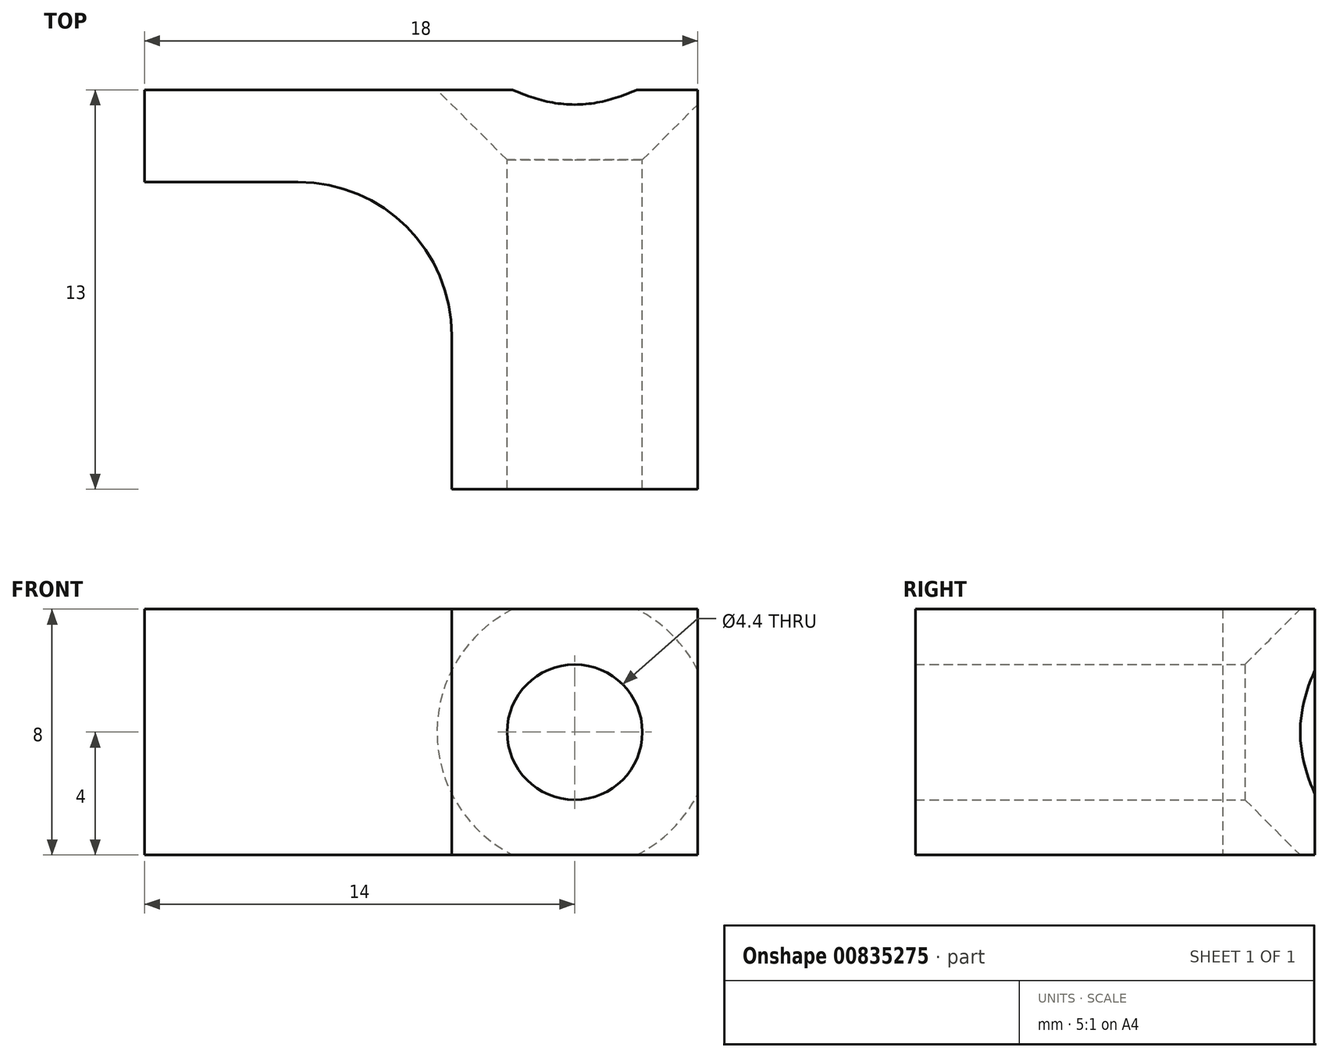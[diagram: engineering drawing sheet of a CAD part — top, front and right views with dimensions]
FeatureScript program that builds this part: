
annotation { "Feature Type Name" : "Feature", "Feature Type Description" : "" }
export const myFeature = defineFeature(function(context is Context, id is Id, definition is map)
    precondition{}
    {
        {
            var Q0;
            Q0=qCreatedBy(makeId("Top.planeOp"),FACE);
            var sketch = newSketch(context, id + "F0", { "sketchPlane" : qUnion([Q0])});
            skLineSegment(sketch, "E0.bottom", {"start": v(-5, 0) * mm, "end": v(-10, 0) * mm});
            skLineSegment(sketch, "E0.top", {"start": v(0, -10) * mm, "end": v(-10, -10) * mm});
            skLineSegment(sketch, "E0.left", {"start": v(0, -5) * mm, "end": v(0, -10) * mm});
            skLineSegment(sketch, "E0.right", {"start": v(-10, 0) * mm, "end": v(-10, -10) * mm});
            skLineSegment(sketch, "E1", {"start": v(-10, 0) * mm, "end": v(-10, 3) * mm});
            skLineSegment(sketch, "E2", {"start": v(-10, 3) * mm, "end": v(8, 3) * mm});
            skLineSegment(sketch, "E3", {"start": v(8, 3) * mm, "end": v(8, -10) * mm});
            skLineSegment(sketch, "E4", {"start": v(8, -10) * mm, "end": v(0, -10) * mm});
            skPoint(sketch, "E5.visualSharp", {"position": v(0, 0) * mm});
            skArc(sketch, "E5.filletArc", {"start": v(0, -5) * mm, "mid": v(-1.46, -1.46) * mm, "end": v(-5, 0) * mm});
            skSolve(sketch);
        }
        {
            var Q0;
            Q0=makeQuery(id+"F0.imprint","IMPRINT",FACE,{"disambiguationData":[TD([[makeQuery(id+"F0.imprint","IMPRINT",EDGE,{"derivedFrom":sQuery(id+"F0.wireOp",EDGE,"E0.bottom")}),-1.0]])]});
            extrude(context, id + "F1", {"entities" : qUnion([Q0]), "depth" : 8 * mm, "offsetDistance" : 25 * mm});
        }
        {
            var Q0;
            Q0=makeQuery(id+"F1.opExtrude","SWEPT_FACE",FACE,{"disambiguationData":[OSD([sQuery(id+"F0.wireOp",EDGE,"E2")])]});
            var sketch = newSketch(context, id + "F2", { "sketchPlane" : qUnion([Q0])});
            skPoint(sketch, "E6", {"position": v(1, 0) * mm});
            skLineSegment(sketch, "E7", {"start": v(-8, 8) * mm, "end": v(0, 0) * mm, "construction": true});
            skPoint(sketch, "E8", {"position": v(-4, 4) * mm});
            skSolve(sketch);
        }
        {
            var Q0;
            Q0=sQuery(id+"F2.wireOp",VERTEX,"E8");
            var Q1;
            Q1=makeQuery(id+"F1.opExtrude","SWEPT_BODY",BODY,{"disambiguationData":[OSD([sQuery(id+"F0.wireOp",EDGE,"E0.bottom"),sQuery(id+"F0.wireOp",EDGE,"E0.left"),sQuery(id+"F0.wireOp",EDGE,"E1"),sQuery(id+"F0.wireOp",EDGE,"E2"),sQuery(id+"F0.wireOp",EDGE,"E3"),sQuery(id+"F0.wireOp",EDGE,"E4"),sQuery(id+"F0.wireOp",EDGE,"E5.filletArc")])]});
            hole(context, id + "F3", {"style" : HoleStyle.C_SINK, "endStyle" : HoleEndStyle.THROUGH, "standardTappedOrClearance" : lookupTablePath({ "fit" : "Normal", "standard" : "ISO", "size" : "M4", "type" : "Clearance" }), "standardBlindInLast" : lookupTablePath({ "fit" : "Standard", "standard" : "ISO", "size" : "M4", "type" : "Clearance" }), "holeDiameter" : 4.4 * mm, "cSinkDiameter" : 8.96 * mm, "cSinkAngle" : 90 * degree, "majorDiameter" : 2.5 * mm, "isTappedThrough" : true, "tappedDepth" : 12 * mm, "tapClearance" : 3, "locations" : qUnion([Q0]), "scope" : qUnion([Q1])});
        }
    });
